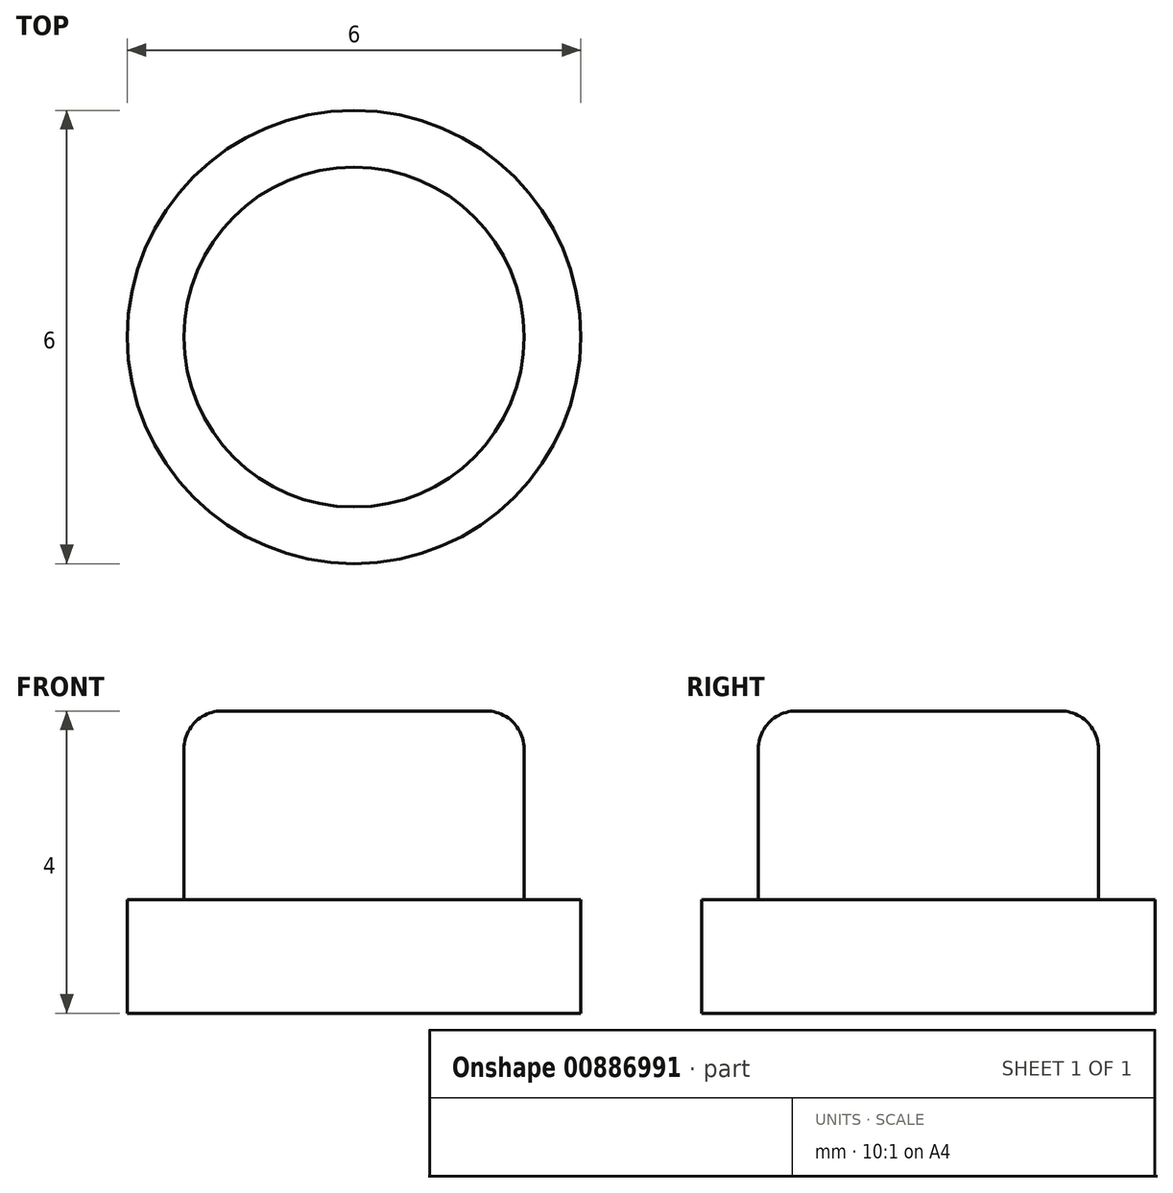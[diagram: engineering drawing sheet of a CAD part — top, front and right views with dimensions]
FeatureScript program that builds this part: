
annotation { "Feature Type Name" : "Feature", "Feature Type Description" : "" }
export const myFeature = defineFeature(function(context is Context, id is Id, definition is map)
    precondition{}
    {
        {
            var Q0;
            Q0=qCreatedBy(makeId("Top.planeOp"),FACE);
            var sketch = newSketch(context, id + "F0", { "sketchPlane" : qUnion([Q0])});
            skCircle(sketch, "E0", {"center": v(0, 0) * mm, "radius": 3 * mm});
            skCircle(sketch, "E1", {"center": v(0, 0) * mm, "radius": 2.25 * mm});
            skSolve(sketch);
        }
        {
            var Q0;
            Q0 = qSketchRegion(id + "F0", true);
            var Q1;
            Q1=makeQuery(id+"F0.imprint","IMPRINT",FACE,{"disambiguationData":[TD([[makeQuery(id+"F0.imprint","IMPRINT",EDGE,{"derivedFrom":sQuery(id+"F0.wireOp",EDGE,"E1")}),1.0]])]});
            extrude(context, id + "F1", {"entities" : qUnion([Q0, Q1]), "depth" : 1.5 * mm, "offsetDistance" : 25 * mm});
        }
        {
            var Q0;
            Q0=makeQuery(id+"F0.imprint","IMPRINT",FACE,{"disambiguationData":[TD([[makeQuery(id+"F0.imprint","IMPRINT",EDGE,{"derivedFrom":sQuery(id+"F0.wireOp",EDGE,"E1")}),1.0]])]});
            extrude(context, id + "F2", {"entities" : qUnion([Q0]), "operationType" : NewBodyOperationType.ADD, "depth" : 4 * mm, "offsetDistance" : 25 * mm});
        }
        {
            var Q0;
            Q0=makeQuery(id+"F2.opExtrude","CAP_FACE",FACE,{"disambiguationData":[OSD([sQuery(id+"F0.wireOp",EDGE,"E1")])],"isStart":false});
            fillet(context, id + "F3", {"entities" : qUnion([Q0]), "radius" : 0.5 * mm, "tangentPropagation" : true, "allowEdgeOverflow" : false});
        }
    });
